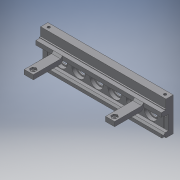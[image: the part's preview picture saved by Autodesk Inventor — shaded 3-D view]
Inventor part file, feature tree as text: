
AUTODESK INVENTOR PART (.ipt)
format: ipt  version: 2016 SP2 (Build 200236200, 236)  size: 307,712 bytes
history: native  units: mm
features: reference x16, extrude x9, sketch x9, chamfer x2, mirror x1, pattern_linear x1
ambient origin geometry x8: Origin, YZ Plane, XZ Plane, XY Plane, X Axis, Y Axis, Z Axis, Center Point
bodies: Volumenkörper1 (feature_tree)
feature tree (38):
  extrude  "Extrusion1"  Depth=4.5mm
  extrude  "Extrusion2"  Depth=3.5mm
  extrude  "Extrusion3"  Depth=15.97mm
  chamfer  "Fase1"  Distance=69.4mm
  chamfer  "Fase2"  Distance=5.0mm
  extrude  "Extrusion4"  Depth=2.0mm TaperAngle=45.0deg
  extrude  "Extrusion5"  Depth=2.0mm TaperAngle=45.0deg
  extrude  "Extrusion6"  Depth=3.5mm
  mirror  "Spiegeln1"
  extrude  "Extrusion9"  Depth=5.0mm
  extrude  "Extrusion10"  Depth=5.0mm
  extrude  "Extrusion11"  Depth=32.25mm TaperAngle=0.0deg
  pattern_linear  "Rechteckige Anordnung1"  Spacing1=34.75mm  [1 undecoded]
  sketch  "Skizze1"  dims[d0=2.0mm d1=4.5mm]
  reference  "Referenz1"
  reference  "Referenz2"
  reference  "Referenz3"
  reference  "Referenz4"
  reference  "Referenz5"
  reference  "Referenz6"
  reference  "Referenz7"
  reference  "Referenz8"
  reference  "Referenz9"
  sketch  "Skizze2"  dims[d2=3.5mm d3=3.47mm]
  reference  "Referenz10"
  sketch  "Skizze3"  dims[d4=15.97mm d5=1.8mm]
  reference  "Referenz11"
  sketch  "Skizze4"  dims[d6=45.0deg]
  sketch  "Skizze6"  dims[d7=135.0deg]
  sketch  "Skizze7"  dims[d8=4.53mm]
  sketch  "Skizze10"  dims[d9=1.8mm]
  reference  "Referenz15"
  reference  "Referenz16"
  reference  "Referenz17"
  reference  "Referenz18"
  sketch  "Skizze11"  dims[d10=4.5mm d11=69.4mm d12=0.0mm d13=5.0mm d14=0.0mm]
  sketch  "Skizze12"  dims[d15=32.25mm d16=0.0mm d17=2.4mm d18=2.0mm d19=45.0deg d20=2.0mm d21=2.0mm d22=45.0deg d23=3.5mm d24=5.0mm d25=5.0mm d26=32.25mm d27=0.0mm d28=34.75mm d29=0.0mm d30=11.25mm d31=0.0mm d51=5.7mm d52=5.7mm d53=2.2mm d54=0.0mm d61=12.0mm d62=19.4mm d63=5.5mm d64=0.0mm d65=15.0mm d66=4.0mm d67=0.0mm d68=60.0mm d70=20.0mm]
  reference  "Referenz19"
note: 1 required parameter value undecoded (feature->parameter linkage not recoverable at this tier; creation-order binding heuristic only, values carry confidence <= 0.55)
